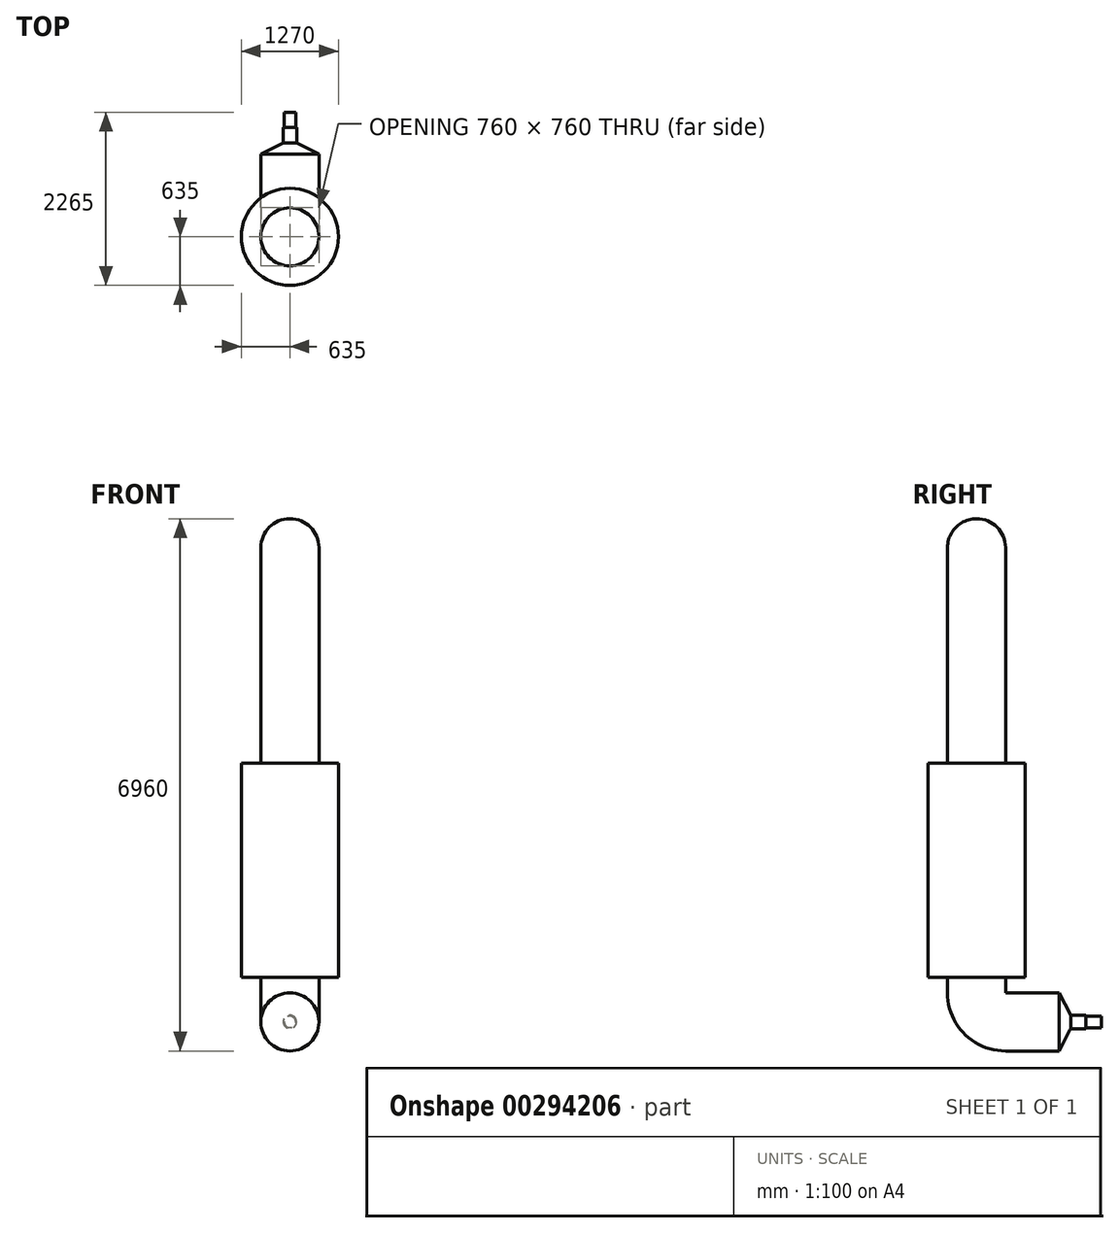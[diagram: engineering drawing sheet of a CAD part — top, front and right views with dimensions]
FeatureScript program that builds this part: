
annotation { "Feature Type Name" : "Feature", "Feature Type Description" : "" }
export const myFeature = defineFeature(function(context is Context, id is Id, definition is map)
    precondition{}
    {
        {
            var Q0;
            Q0=qCreatedBy(makeId("Front.planeOp"),FACE);
            var sketch = newSketch(context, id + "F0", { "sketchPlane" : qUnion([Q0])});
            skCircle(sketch, "E0", {"center": v(0, 0) * mm, "radius": 75 * mm});
            skSolve(sketch);
        }
        {
            var Q0;
            Q0=makeQuery(id+"F0.imprint","IMPRINT",FACE,{"disambiguationData":[TD([[makeQuery(id+"F0.imprint","IMPRINT",EDGE,{"derivedFrom":sQuery(id+"F0.wireOp",EDGE,"E0")}),1.0]])]});
            extrude(context, id + "F1", {"entities" : qUnion([Q0]), "depth" : 200 * mm});
        }
        {
            var Q0;
            Q0=makeQuery(id+"F1.opExtrude","CAP_FACE",FACE,{"disambiguationData":[OSD([sQuery(id+"F0.wireOp",EDGE,"E0")])],"isStart":false});
            var sketch = newSketch(context, id + "F2", { "sketchPlane" : qUnion([Q0])});
            skCircle(sketch, "E1", {"center": v(0, 0) * mm, "radius": 87.5 * mm});
            skSolve(sketch);
        }
        {
            var Q0;
            Q0=makeQuery(id+"F2.imprint","IMPRINT",FACE,{"disambiguationData":[TD([[makeQuery(id+"F2.imprint","IMPRINT",EDGE,{"derivedFrom":sQuery(id+"F2.wireOp",EDGE,"E1")}),1.0]])]});
            var Q1;
            Q1=makeQuery(id+"F2.imprint","IMPRINT",FACE,{"disambiguationData":[TD([[makeQuery(id+"F2.imprint","IMPRINT",EDGE,{"derivedFrom":makeQuery(id+"F1.opExtrude","CAP_EDGE",EDGE,{"disambiguationData":[OSD([sQuery(id+"F0.wireOp",EDGE,"E0")])],"isStart":false})}),1.0]])]});
            extrude(context, id + "F3", {"entities" : qUnion([Q0, Q1]), "operationType" : NewBodyOperationType.ADD, "depth" : 200 * mm});
        }
        {
            var Q0;
            Q0=makeQuery(id+"F3.opExtrude","CAP_FACE",FACE,{"disambiguationData":[OSD([sQuery(id+"F2.wireOp",EDGE,"E1")])],"isStart":false});
            cPlane(context, id + "F4", {"entities" : qUnion([Q0]), "cplaneType" : CPlaneType.OFFSET, "offset" : 150 * mm, "width" : 150 * mm, "height" : 150 * mm});
        }
        {
            var Q0;
            Q0=qCreatedBy(id+"F4.planeOp",FACE);
            var sketch = newSketch(context, id + "F5", { "sketchPlane" : qUnion([Q0])});
            skCircle(sketch, "E2", {"center": v(0, 0) * mm, "radius": 380 * mm});
            skSolve(sketch);
        }
        {
            var Q1;
            Q1=makeQuery(id+"F3.opExtrude","CAP_FACE",FACE,{"disambiguationData":[OSD([sQuery(id+"F2.wireOp",EDGE,"E1")])],"isStart":false});
            var Q2;
            Q2=makeQuery(id+"F5.imprint","IMPRINT",FACE,{"disambiguationData":[TD([[makeQuery(id+"F5.imprint","IMPRINT",EDGE,{"derivedFrom":sQuery(id+"F5.wireOp",EDGE,"E2")}),1.0]])]});
            loft(context, id + "F6", {"operationType" : NewBodyOperationType.ADD, "sheetProfilesArray" : [{ "sheetProfileEntities" : qUnion([Q1]) }, { "sheetProfileEntities" : qUnion([Q2]) }]});
        }
        {
            var Q0;
            Q0=makeQuery(id+"F6.opLoft","CAP_FACE",FACE,{"disambiguationData":[OSD([makeQuery(id+"F5.imprint","IMPRINT",FACE,{"disambiguationData":[TD([[makeQuery(id+"F5.imprint","IMPRINT",EDGE,{"derivedFrom":sQuery(id+"F5.wireOp",EDGE,"E2")}),1.0]])]})])],"isStart":true});
            extrude(context, id + "F7", {"entities" : qUnion([Q0]), "operationType" : NewBodyOperationType.ADD, "depth" : 700 * mm});
        }
        {
            var Q0;
            Q0=makeQuery(id+"F7.opExtrude","CAP_FACE",FACE,{"disambiguationData":[OSD([makeQuery(id+"F5.imprint","IMPRINT",FACE,{"disambiguationData":[TD([[makeQuery(id+"F5.imprint","IMPRINT",EDGE,{"derivedFrom":sQuery(id+"F5.wireOp",EDGE,"E2")}),1.0]])]})])],"isStart":false});
            var sketch = newSketch(context, id + "F8", { "sketchPlane" : qUnion([Q0])});
            skPoint(sketch, "E3", {"position": v(0, 0) * mm});
            skPoint(sketch, "E4", {"position": v(0, 380) * mm});
            skCircle(sketch, "E5", {"center": v(0, 0) * mm, "radius": 380 * mm});
            skSolve(sketch);
        }
        {
            var Q0;
            Q0=qCreatedBy(makeId("Right.planeOp"),FACE);
            var sketch = newSketch(context, id + "F9", { "sketchPlane" : qUnion([Q0])});
            skArc(sketch, "E6", {"start": v(-1250, 0) * mm, "mid": v(-1518.7, 111.3) * mm, "end": v(-1630, 380) * mm});
            skLineSegment(sketch, "E7", {"start": v(-1250, 380) * mm, "end": v(-1514.79, 380) * mm, "construction": true});
            skSolve(sketch);
        }
        {
            var Q0;
            Q0=makeQuery(id+"F8.imprint","IMPRINT",FACE,{"disambiguationData":[TD([[makeQuery(id+"F8.imprint","IMPRINT",EDGE,{"derivedFrom":sQuery(id+"F8.wireOp",EDGE,"E5")}),1.0]])]});
            var Q1;
            Q1=sQuery(id+"F9.wireOp",EDGE,"E6");
            sweep(context, id + "F10", {"operationType" : NewBodyOperationType.ADD, "profiles" : qUnion([Q0]), "path" : qUnion([Q1])});
        }
        {
            var Q0;
            Q0=makeQuery(id+"F10.opSweep","CAP_FACE",FACE,{"disambiguationData":[OSD([sQuery(id+"F8.wireOp",EDGE,"E5"),sQuery(id+"F9.wireOp",VERTEX,"E6.end")])],"isStart":false});
            var sketch = newSketch(context, id + "F11", { "sketchPlane" : qUnion([Q0])});
            skCircle(sketch, "E8", {"center": v(0, -1630) * mm, "radius": 380 * mm});
            skSolve(sketch);
        }
        {
            var Q0;
            Q0=makeQuery(id+"F11.imprint","IMPRINT",FACE,{"disambiguationData":[TD([[makeQuery(id+"F11.imprint","IMPRINT",EDGE,{"derivedFrom":sQuery(id+"F11.wireOp",EDGE,"E8")}),1.0]])]});
            extrude(context, id + "F12", {"entities" : qUnion([Q0]), "operationType" : NewBodyOperationType.ADD, "depth" : 200 * mm});
        }
        {
            var Q0;
            Q0=makeQuery(id+"F12.opExtrude","CAP_FACE",FACE,{"disambiguationData":[OSD([sQuery(id+"F11.wireOp",EDGE,"E8")])],"isStart":false});
            var sketch = newSketch(context, id + "F13", { "sketchPlane" : qUnion([Q0])});
            skCircle(sketch, "E9", {"center": v(0, -1630) * mm, "radius": 635 * mm});
            skSolve(sketch);
        }
        {
            var Q0;
            Q0=makeQuery(id+"F13.imprint","IMPRINT",FACE,{"disambiguationData":[TD([[makeQuery(id+"F13.imprint","IMPRINT",EDGE,{"derivedFrom":sQuery(id+"F13.wireOp",EDGE,"E9")}),1.0]])]});
            var Q1;
            Q1=makeQuery(id+"F13.imprint","IMPRINT",FACE,{"disambiguationData":[TD([[makeQuery(id+"F13.imprint","IMPRINT",EDGE,{"derivedFrom":makeQuery(id+"F12.opExtrude","CAP_EDGE",EDGE,{"disambiguationData":[OSD([sQuery(id+"F11.wireOp",EDGE,"E8")])],"isStart":false})}),1.0]])]});
            extrude(context, id + "F14", {"entities" : qUnion([Q0, Q1]), "operationType" : NewBodyOperationType.ADD, "depth" : 2800 * mm});
        }
        {
            var Q0;
            Q0=makeQuery(id+"F14.opExtrude","CAP_FACE",FACE,{"disambiguationData":[OSD([sQuery(id+"F13.wireOp",EDGE,"E9")])],"isStart":false});
            var sketch = newSketch(context, id + "F15", { "sketchPlane" : qUnion([Q0])});
            skCircle(sketch, "E10", {"center": v(0, -1630) * mm, "radius": 380 * mm});
            skSolve(sketch);
        }
        {
            var Q0;
            Q0=makeQuery(id+"F15.imprint","IMPRINT",FACE,{"disambiguationData":[TD([[makeQuery(id+"F15.imprint","IMPRINT",EDGE,{"derivedFrom":sQuery(id+"F15.wireOp",EDGE,"E10")}),1.0]])]});
            extrude(context, id + "F16", {"entities" : qUnion([Q0]), "operationType" : NewBodyOperationType.ADD, "depth" : 3200 * mm});
        }
        {
            var Q0;
            Q0=makeQuery(id+"F16.opExtrude","CAP_FACE",FACE,{"disambiguationData":[OSD([sQuery(id+"F15.wireOp",EDGE,"E10")])],"isStart":false});
            fillet(context, id + "F17", {"entities" : qUnion([Q0]), "radius" : 380 * mm, "tangentPropagation" : true, "allowEdgeOverflow" : false});
        }
    });
